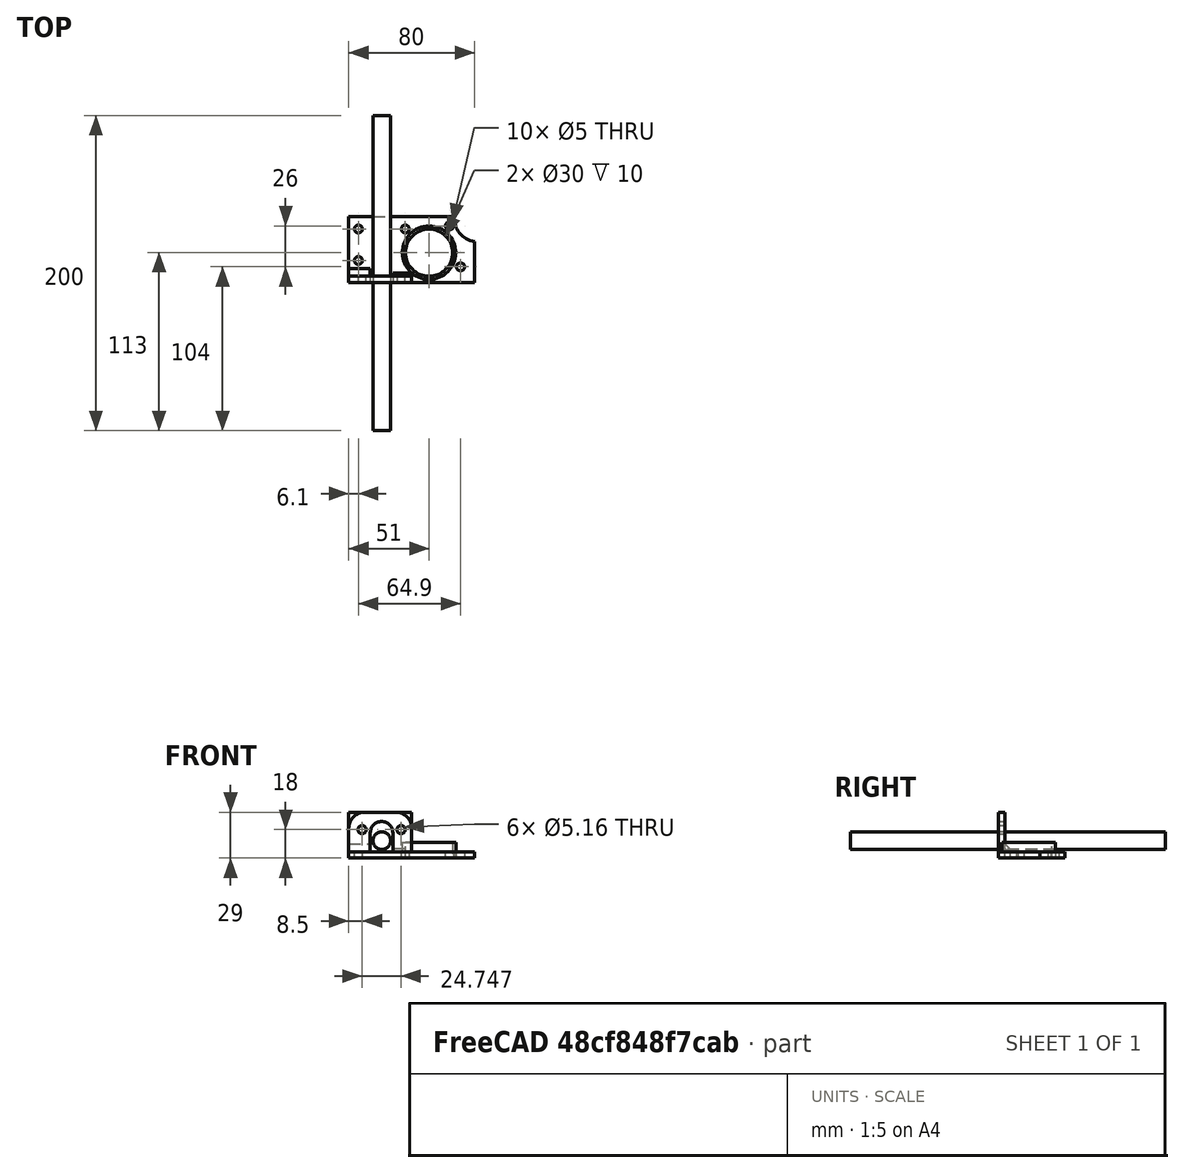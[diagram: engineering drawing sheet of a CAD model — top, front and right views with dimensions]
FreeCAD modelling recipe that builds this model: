
FCSTD DOCUMENT  (FreeCAD 0.14R3700 (Git))
Label: armBaseFlangeMount
License: CC-BY 3.0
LicenseURL: http://creativecommons.org/licenses/by/3.0/
objects: Mesh::Feature×2, Sketcher::SketchObject×2, PartDesign::Pocket×2, PartDesign::Chamfer×2, Part::Cylinder×1, Part::Box×1, PartDesign::Fillet×1, Part::MultiFuse×1, Part::Feature×1
note: 13 computed .brp shape members not serialized (recipe doc carries the construction recipe); baked Part::Feature solids carry a one-line shape summary decoded from their .brp

FEATURE [Mesh::Feature] tmp  label="plate"
FEATURE [Mesh::Feature] lead_screw_flange  label="lead-screw-flange"
  Placement = pos=(-747,556,-523) rot=(0,0.707107,0.707107;3.14159rad)
FEATURE [Part::Cylinder] Cylinder001  label="lead_screw"
  Angle = 360
  Height = 200
  Placement = pos=(-747,700,-523) rot=(1,0,0;1.5708rad)
  Radius = 5.556
FEATURE [Part::Box] Box001  label="Cube001"
  Height = 25
  Length = 40
  Placement = pos=(-768,594,-530) rot=(0,0,1;0rad)
  Width = 4
FEATURE [Sketcher::SketchObject] Sketch002
  Placement = pos=(-768,598,-530) rot=(0,0.707107,0.707107;3.14159rad)
  Support = -> Box001 [Face4]
  sketch-geometry (6):
    g0: Circle CenterX=-33.247 CenterY=14 CenterZ=0 NormalX=0 NormalY=0 NormalZ=1 Radius=2.5781
    g1: Circle CenterX=-8.5 CenterY=14 CenterZ=0 NormalX=0 NormalY=0 NormalZ=1 Radius=2.5781
    g2: ArcOfCircle CenterX=-20.85 CenterY=12 CenterZ=0 NormalX=0 NormalY=0 NormalZ=1 Radius=7.15 StartAngle=0 EndAngle=3.14159
    g3: LineSegment StartX=-13.7 StartY=12 StartZ=0 EndX=-13.7 EndY=0 EndZ=0
    g4: LineSegment StartX=-28 StartY=12 StartZ=0 EndX=-28 EndY=0 EndZ=0
    g5: LineSegment StartX=-28 StartY=0 StartZ=0 EndX=-13.7 EndY=0 EndZ=0
  constraints (21):
    c: Radius(g0) = 2.5781
    c: Equal(g0,g1)
    c: DistanceY(g-1,g0) = 14
    c: DistanceY(g-1,g1) = 14
    c: DistanceX(g0,g1) = 24.747
    c: DistanceX(g-1,g1) = -8.5
    c: DistanceY(g-1,g2) = 12
    c: DistanceX(g-1,g2) = -20.85
    c: DistanceY(g-1,g2) = 12
    c: DistanceY(g-1,g2) = 12
    c: DistanceX(g-1,g2) = -28
    c: PointOnObject(g3,g-1)
    c: Vertical(g3)
    c: Tangent(g3,g2)
    c: PointOnObject(g4,g-1)
    c: Vertical(g4)
    c: Tangent(g4,g2)
    c: Coincident(g2,g4)
    c: Coincident(g3,g2)
    c: Coincident(g5,g4)
    c: Coincident(g5,g3)
FEATURE [PartDesign::Pocket] Pocket002
  Length = 5
  Placement = pos=(-768,594,-530) rot=(0,0,1;0rad)
  Sketch = -> Sketch002
  Type = 1
FEATURE [PartDesign::Fillet] Fillet
  Base = -> Pocket002 [Edge15]
  Placement = pos=(-768,594,-530) rot=(0,0,1;0rad)
  Radius = 10
FEATURE [Sketcher::SketchObject] Sketch005
  Placement = pos=(-768,594,-530) rot=(0,0,1;0rad)
  sketch-geometry (4):
    g0: Circle CenterX=6.1 CenterY=34 CenterZ=0 NormalX=0 NormalY=0 NormalZ=1 Radius=2.5
    g1: Circle CenterX=6.1 CenterY=14 CenterZ=0 NormalX=0 NormalY=0 NormalZ=1 Radius=2.5
    g2: Circle CenterX=35.9 CenterY=34 CenterZ=0 NormalX=0 NormalY=0 NormalZ=1 Radius=2.5
    g3: Circle CenterX=35.9 CenterY=14 CenterZ=0 NormalX=0 NormalY=0 NormalZ=1 Radius=2.5
  constraints (12):
    c: Radius(g0) = 2.5
    c: Equal(g0,g1)
    c: Equal(g1,g2)
    c: DistanceY(g-1,g1) = 14
    c: DistanceY(g1,g0) = 20
    c: DistanceY(g-1,g2) = 34
    c: DistanceX(g-1,g0) = 6.1
    c: DistanceX(g-1,g1) = 6.1
    c: DistanceX(g-1,g2) = 35.9
    c: DistanceX(g3,g2) = 0
    c: DistanceY(g3,g1) = 0
    c: Equal(g3,g1)
FEATURE [PartDesign::Pocket] Pocket004
  Length = 5
  Placement = pos=(-768,594,-534) rot=(0,0,1;0rad)
  Sketch = -> Sketch005
  Type = 1
FEATURE [Part::MultiFuse] Fusion
  Shapes = -> [Pocket004]
FEATURE [PartDesign::Chamfer] Chamfer
  Base = -> Fusion [Edge42]
  Size = 5
FEATURE [PartDesign::Chamfer] Chamfer001
  Base = -> Chamfer [Edge17]
  Size = 2
FEATURE [Part::Feature] Chamfer001001  label="Chamfer002"
  shape: bbox 80 x 42 x 29 mm, 27 faces (baked)
